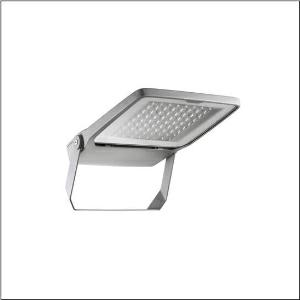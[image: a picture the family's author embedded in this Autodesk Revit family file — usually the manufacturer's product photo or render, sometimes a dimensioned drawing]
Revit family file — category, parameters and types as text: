
# Revit family: floodlight_fl_20_mini___rs17_5xa7671b2b1ac_3d4d
name_source: partatom
category: Lighting Fixtures
units: mm (PartAtom-declared; Revit-internal decimal feet)

## family parameters
Cut with Voids When Loaded = No
Host = Face
Light Source = No
Part Type = Normal
Room Calculation Point = No
Round Connector Dimension = Use Diameter
Shared = No

## types (1)
- Floodlight FL 20 mini  RS17 (1 x LED 4000K / CRI = 70 (unbekannt), 6810 lm, 4000K)
    Apparent Load = 51 VA
    CIE Flux Codes = 79 92 99 100 100
    Color Rendering = 70
    Color Temperature = 4000K
    Default Elevation = 1800 mm
    Description = Floodlight FL 20 mini, floodlight, primary light control with lens, of plastic, primary optical cover: protective disc, of toughened safety glass, transparent, light distribution: RS17, light emission: direct distribution, primary light characteristic: rotationally symmetric, installation type: surface-mounted, LED, High Power LED, rated luminous flux: 6.810lm, luminous efficacy: 134lm/W, light colour: 740, colour temperature: 4000K, control gear: ECG Basic, control: power reduction, overheat protection, electronic power reduction, with terminal, 5-pole, max. 2.5mm², mains connection: 220..240V, AC, 50/60Hz, rated input power: 51W, LED unit, of diecast aluminium, powder-coated, Siteco® metallic grey (DB 702S), corrosivity category C5 mid according to DIN EN ISO 12944, incl. 1x M20 cable gland for cable Ø 6.5..12mm, length: 446mm, width: 355mm, height: 62mm, housing frame, of diecast aluminium, powder-coated, Siteco® metallic grey (DB 702S), mounting bracket, of steel, powder-coated, Siteco® metallic grey (DB 702S), ON/OFF, protection rating (complete): IP66, insulation class (complete): insulation class I (protective earthing), certification: CE, ENEC, VDE, protection symbol: D, permissible operating ambient temperature: -40..+40°C, permissible operating ambient temperature for outdoor applications: -40..+50°C, standard: DIN EN 12944, packaging unit: 1 piece

Light Distribution: RS17
    Height = 62 mm  [stored 0.203412 ft]
    Lamp = 1 x LED 4000K / CRI >= 70 (unbekannt)
    Lamp Light Flux = 6810 lm
    Lamp count = 1
    Length = 467 mm
    Luminous efficacy = 134 lm/W
    Manufacturer = Siteco
    ModVariant = No
    Model = 5XA7671B2B1AC
    Mounting Place = Wall
    Mounting Type = Surface mounted
    Number of Poles = 1
    OnlyDefault = Yes
    Power Factor = 1
    Product Name = Floodlight FL 20 mini | RS17
    Product group = floodlight | wall mounted
    ProductGroupID = 2001
    Protection Class = Protection class I
    Protection Degree = IP 66
    RLX_Detail_Level = 1
    RLX_Emergency_Light_Flux = 0 lm
    RLX_Emergency_Type = 0
    RLX_Emergency_Type_DB = No
    RlxData = <blob elided: 66001 chars, md5=3e85921c>
    Socket = socket
    Standby Power = 0 W
    System Light Flux = 6810 lm
    System Power = 51 W
    Type Comments = Product without accessories
    Type Image = l_1005948.jpg
    URL = http://relux.com
    VarID = ---
    Voltage = 0 V
    Weight = 0.00 kg
    Width = 335 mm

note: [stored X ft] marks values corroborated as IEEE doubles in the binary element streams (Revit-internal decimal feet)

## geometry (parser evidence)
native form markers: Blend x4, Sweep x12
no freeform markers — native parametric forms only
